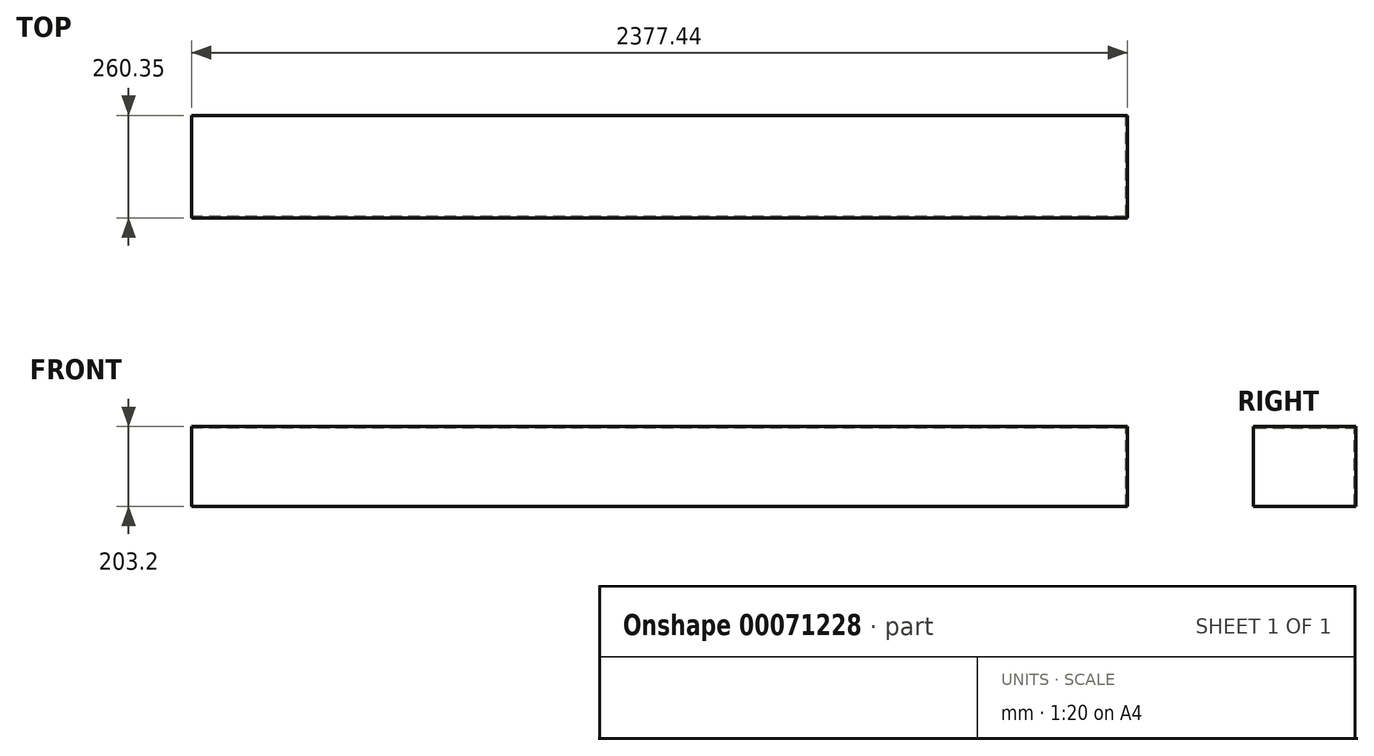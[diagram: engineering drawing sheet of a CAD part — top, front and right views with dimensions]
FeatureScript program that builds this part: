
annotation { "Feature Type Name" : "Feature", "Feature Type Description" : "" }
export const myFeature = defineFeature(function(context is Context, id is Id, definition is map)
    precondition{}
    {
        {
            var Q0;
            Q0=qCreatedBy(makeId("Front.planeOp"),FACE);
            var sketch = newSketch(context, id + "F0", { "sketchPlane" : qUnion([Q0])});
            skLineSegment(sketch, "E0.bottom", {"start": v(0, 0) * mm, "end": v(-2377.44, 0) * mm});
            skLineSegment(sketch, "E0.top", {"start": v(0, 203.2) * mm, "end": v(-2377.44, 203.2) * mm});
            skLineSegment(sketch, "E0.left", {"start": v(0, 0) * mm, "end": v(0, 203.2) * mm});
            skLineSegment(sketch, "E0.right", {"start": v(-2377.44, 0) * mm, "end": v(-2377.44, 203.2) * mm});
            skSolve(sketch);
        }
        {
            var Q0;
            Q0=makeQuery(id+"F0.imprint","IMPRINT",FACE,{"disambiguationData":[TD([[makeQuery(id+"F0.imprint","IMPRINT",EDGE,{"derivedFrom":sQuery(id+"F0.wireOp",EDGE,"E0.bottom")}),-1.0]])]});
            extrude(context, id + "F1", {"entities" : qUnion([Q0]), "depth" : 260.35 * mm});
        }
        {
            var Q0;
            Q0=makeQuery(id+"F1.opExtrude","SWEPT_FACE",FACE,{"disambiguationData":[OSD([sQuery(id+"F0.wireOp",EDGE,"E0.bottom")])]});
            shell(context, id + "F2", {"entities" : qUnion([Q0]), "thickness" : 3.17 * mm});
        }
    });
